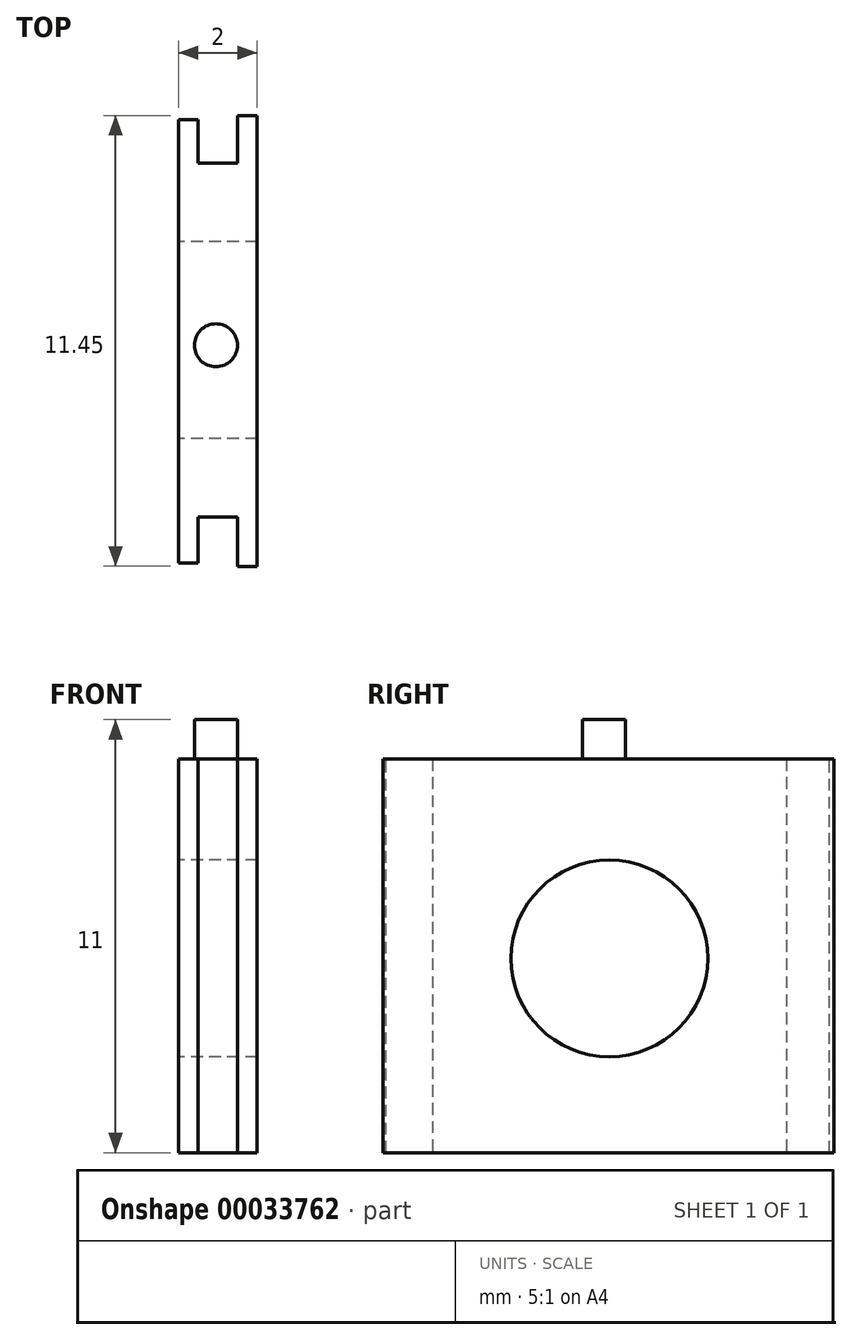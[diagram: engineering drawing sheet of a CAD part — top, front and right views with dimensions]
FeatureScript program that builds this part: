
annotation { "Feature Type Name" : "Feature", "Feature Type Description" : "" }
export const myFeature = defineFeature(function(context is Context, id is Id, definition is map)
    precondition{}
    {
        {
            var Q0;
            Q0=qCreatedBy(makeId("Right.planeOp"),FACE);
            var sketch = newSketch(context, id + "F0", { "sketchPlane" : qUnion([Q0])});
            skLineSegment(sketch, "E0.bottom", {"start": v(-20.01, 10) * mm, "end": v(-11.02, 10) * mm});
            skLineSegment(sketch, "E0.top", {"start": v(-20.01, 0) * mm, "end": v(-11.02, 0) * mm});
            skLineSegment(sketch, "E0.left", {"start": v(-20.01, 10) * mm, "end": v(-20.01, 0) * mm});
            skLineSegment(sketch, "E0.right", {"start": v(-11.02, 10) * mm, "end": v(-11.02, 0) * mm});
            skSolve(sketch);
        }
        {
            var Q0;
            Q0 = qSketchRegion(id + "F0", true);
            var Q1;
            Q1=makeQuery(id+"F0.imprint","IMPRINT",FACE,{"disambiguationData":[TD([[makeQuery(id+"F0.imprint","IMPRINT",EDGE,{"derivedFrom":sQuery(id+"F0.wireOp",EDGE,"E0.bottom")}),-1.0]])]});
            extrude(context, id + "F1", {"entities" : qUnion([Q0, Q1]), "depth" : 1 * mm});
        }
        {
            var Q0;
            Q0=makeQuery(id+"F1.opExtrude","CAP_FACE",FACE,{"disambiguationData":[OSD([sQuery(id+"F0.wireOp",EDGE,"E0.bottom"),sQuery(id+"F0.wireOp",EDGE,"E0.top"),sQuery(id+"F0.wireOp",EDGE,"E0.left"),sQuery(id+"F0.wireOp",EDGE,"E0.right")])],"isStart":false});
            var sketch = newSketch(context, id + "F2", { "sketchPlane" : qUnion([Q0])});
            skLineSegment(sketch, "E1.bottom", {"start": v(-21.27, 10) * mm, "end": v(-9.82, 10) * mm});
            skLineSegment(sketch, "E1.top", {"start": v(-21.27, 0) * mm, "end": v(-9.82, 0) * mm});
            skLineSegment(sketch, "E1.left", {"start": v(-21.27, 10) * mm, "end": v(-21.27, 0) * mm});
            skLineSegment(sketch, "E1.right", {"start": v(-9.82, 10) * mm, "end": v(-9.82, 0) * mm});
            skSolve(sketch);
        }
        {
            var Q0;
            {var subQ0=sQuery(id+"F2.wireOp",EDGE,"E1.left");Q0=makeQuery(id+"F2.imprint","IMPRINT",FACE,{"disambiguationData":[TD([[makeQuery(id+"F2.imprint","IMPRINT",EDGE,{"derivedFrom":subQ0}),1.0]])]});}
            var Q1;
            {var subQ0=sQuery(id+"F2.wireOp",EDGE,"E1.right");Q1=makeQuery(id+"F2.imprint","IMPRINT",FACE,{"disambiguationData":[TD([[makeQuery(id+"F2.imprint","IMPRINT",EDGE,{"derivedFrom":subQ0}),-1.0]])]});}
            var Q2;
            {var subQ2=makeQuery(id+"F1.opExtrude","CAP_EDGE",EDGE,{"disambiguationData":[OSD([sQuery(id+"F0.wireOp",EDGE,"E0.left")])],"isStart":false});Q2=makeQuery(id+"F2.imprint","IMPRINT",FACE,{"disambiguationData":[TD([[makeQuery(id+"F2.imprint","IMPRINT",EDGE,{"derivedFrom":subQ2}),1.0]])]});}
            extrude(context, id + "F3", {"entities" : qUnion([Q0, Q1, Q2]), "operationType" : NewBodyOperationType.ADD, "depth" : 0.5 * mm});
        }
        {
            var Q0;
            Q0=makeQuery(id+"F1.opExtrude","CAP_FACE",FACE,{"disambiguationData":[OSD([sQuery(id+"F0.wireOp",EDGE,"E0.bottom"),sQuery(id+"F0.wireOp",EDGE,"E0.top"),sQuery(id+"F0.wireOp",EDGE,"E0.left"),sQuery(id+"F0.wireOp",EDGE,"E0.right")])],"isStart":true});
            var sketch = newSketch(context, id + "F4", { "sketchPlane" : qUnion([Q0])});
            skLineSegment(sketch, "E2.bottom", {"start": v(9.93, 0) * mm, "end": v(21.2, 0) * mm});
            skLineSegment(sketch, "E2.top", {"start": v(9.93, 10) * mm, "end": v(21.2, 10) * mm});
            skLineSegment(sketch, "E2.left", {"start": v(9.93, 0) * mm, "end": v(9.93, 10) * mm});
            skLineSegment(sketch, "E2.right", {"start": v(21.2, 0) * mm, "end": v(21.2, 10) * mm});
            skSolve(sketch);
        }
        {
            var Q0;
            {var subQ2=sQuery(id+"F4.wireOp",EDGE,"E2.left");Q0=makeQuery(id+"F4.imprint","IMPRINT",FACE,{"disambiguationData":[TD([[makeQuery(id+"F4.imprint","IMPRINT",EDGE,{"derivedFrom":subQ2}),-1.0]])]});}
            var Q1;
            {var subQ1=makeQuery(id+"F1.opExtrude","CAP_EDGE",EDGE,{"disambiguationData":[OSD([sQuery(id+"F0.wireOp",EDGE,"E0.left")])],"isStart":true});Q1=makeQuery(id+"F4.imprint","IMPRINT",FACE,{"disambiguationData":[TD([[makeQuery(id+"F4.imprint","IMPRINT",EDGE,{"derivedFrom":subQ1}),-1.0]])]});}
            var Q2;
            {var subQ1=sQuery(id+"F4.wireOp",EDGE,"E2.right");Q2=makeQuery(id+"F4.imprint","IMPRINT",FACE,{"disambiguationData":[TD([[makeQuery(id+"F4.imprint","IMPRINT",EDGE,{"derivedFrom":subQ1}),1.0]])]});}
            extrude(context, id + "F5", {"entities" : qUnion([Q0, Q1, Q2]), "operationType" : NewBodyOperationType.ADD, "depth" : 0.5 * mm});
        }
        {
            var Q0;
            Q0=makeQuery(id+"F5.opExtrude","CAP_FACE",FACE,{"disambiguationData":[OSD([sQuery(id+"F4.wireOp",EDGE,"E2.bottom"),sQuery(id+"F4.wireOp",EDGE,"E2.top"),sQuery(id+"F4.wireOp",EDGE,"E2.left"),sQuery(id+"F4.wireOp",EDGE,"E2.right")])],"isStart":false});
            var sketch = newSketch(context, id + "F6", { "sketchPlane" : qUnion([Q0])});
            skCircle(sketch, "E3", {"center": v(15.52, 4.93) * mm, "radius": 0.75 * mm});
            skSolve(sketch);
        }
        {
            var Q0;
            Q0=sQuery(id+"F6.wireOp",VERTEX,"E3.center");
            var Q1;
            Q1=makeQuery(id+"F1.opExtrude","SWEPT_BODY",BODY,{"disambiguationData":[OSD([sQuery(id+"F0.wireOp",EDGE,"E0.bottom"),sQuery(id+"F0.wireOp",EDGE,"E0.top"),sQuery(id+"F0.wireOp",EDGE,"E0.left"),sQuery(id+"F0.wireOp",EDGE,"E0.right")])]});
            hole(context, id + "F7", {"style" : HoleStyle.SIMPLE, "holeDiameter" : 5 * mm, "endStyle" : HoleEndStyle.THROUGH, "locations" : qUnion([Q0]), "scope" : qUnion([Q1])});
        }
        {
            var Q0;
            Q0=makeQuery(id+"F5.boolean.opBoolean","MERGE",FACE,{"derivedFrom":[makeQuery(id+"F3.boolean.opBoolean","MERGE",FACE,{"derivedFrom":[makeQuery(id+"F1.opExtrude","SWEPT_FACE",FACE,{"disambiguationData":[OSD([sQuery(id+"F0.wireOp",EDGE,"E0.bottom")])]}),makeQuery(id+"F3.opExtrude","SWEPT_FACE",FACE,{"disambiguationData":[OSD([sQuery(id+"F2.wireOp",EDGE,"E1.bottom")])]})]}),makeQuery(id+"F5.opExtrude","SWEPT_FACE",FACE,{"disambiguationData":[OSD([sQuery(id+"F4.wireOp",EDGE,"E2.top")])]})]});
            var sketch = newSketch(context, id + "F8", { "sketchPlane" : qUnion([Q0])});
            skCircle(sketch, "E4", {"center": v(0.45, -15.66) * mm, "radius": 0.55 * mm});
            skSolve(sketch);
        }
        {
            var Q0;
            Q0=makeQuery(id+"F8.imprint","IMPRINT",FACE,{"disambiguationData":[TD([[makeQuery(id+"F8.imprint","IMPRINT",EDGE,{"derivedFrom":sQuery(id+"F8.wireOp",EDGE,"E4")}),1.0]])]});
            extrude(context, id + "F9", {"entities" : qUnion([Q0]), "operationType" : NewBodyOperationType.ADD, "depth" : 1 * mm});
        }
    });
